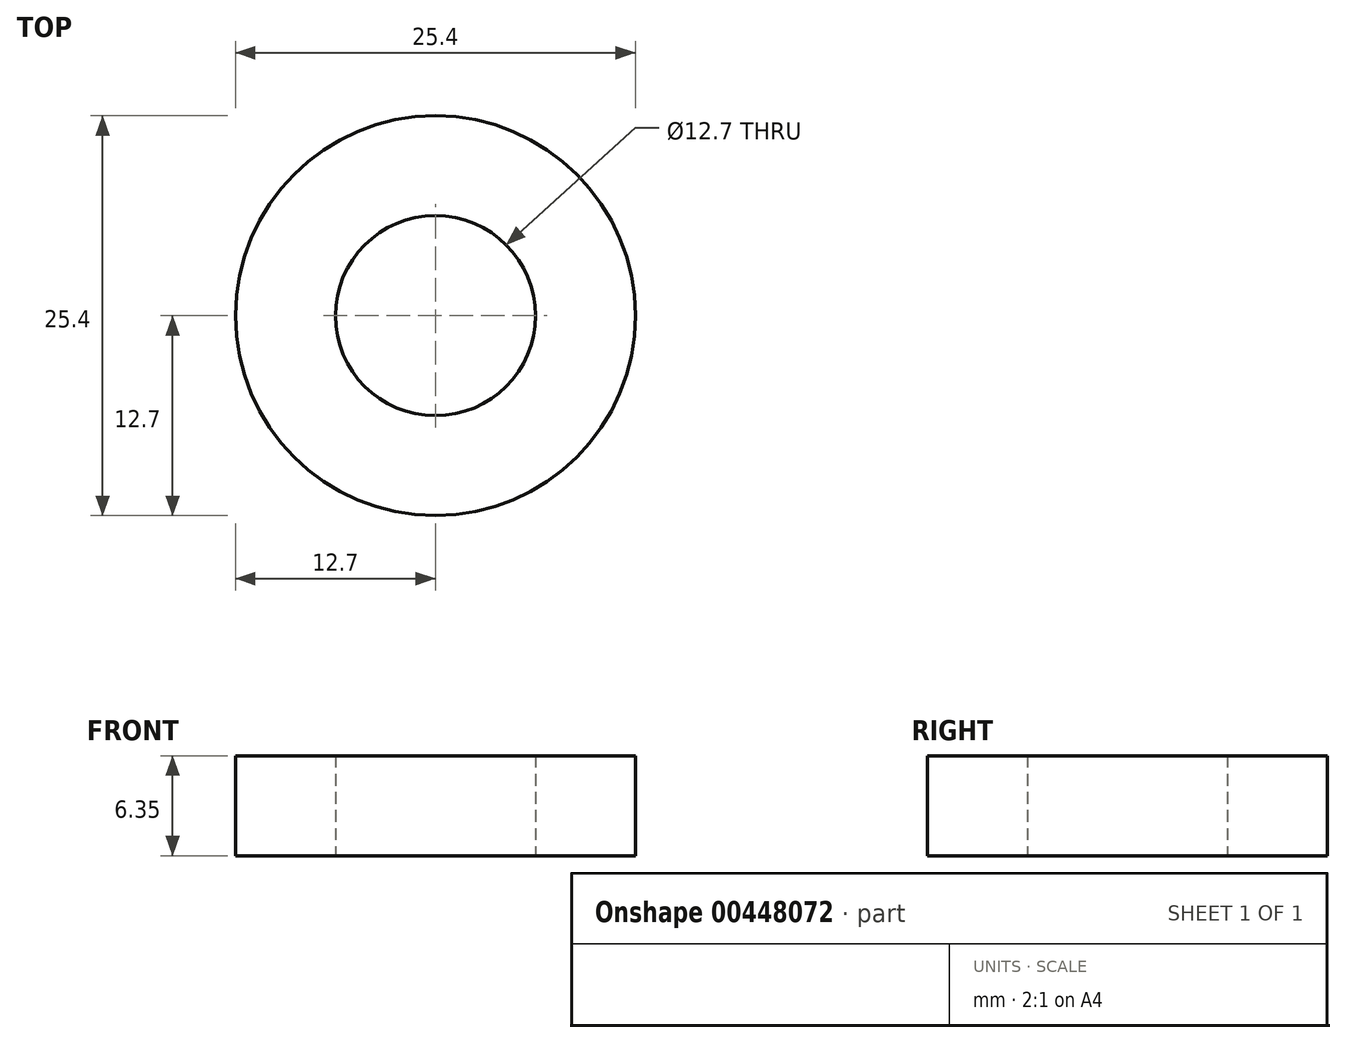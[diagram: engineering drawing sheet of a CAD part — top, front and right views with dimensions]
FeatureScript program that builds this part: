
annotation { "Feature Type Name" : "Feature", "Feature Type Description" : "" }
export const myFeature = defineFeature(function(context is Context, id is Id, definition is map)
    precondition{}
    {
        {
            var Q0;
            Q0=qCreatedBy(makeId("Top.planeOp"),FACE);
            var sketch = newSketch(context, id + "F0", { "sketchPlane" : qUnion([Q0])});
            skCircle(sketch, "E0", {"center": v(0, 0) * mm, "radius": 6.35 * mm});
            skCircle(sketch, "E1", {"center": v(0, 0) * mm, "radius": 12.7 * mm});
            skCircle(sketch, "E2.cCircle", {"center": v(0, 0) * mm, "radius": 6.35 * mm, "construction": true});
            skPoint(sketch, "E2.0.midPoint", {"position": v(0, 6.35) * mm});
            skSolve(sketch);
        }
        {
            var Q0;
            Q0 = qSketchRegion(id + "F0", true);
            extrude(context, id + "F1", {"entities" : qUnion([Q0]), "depth" : 6.35 * mm});
        }
    });
